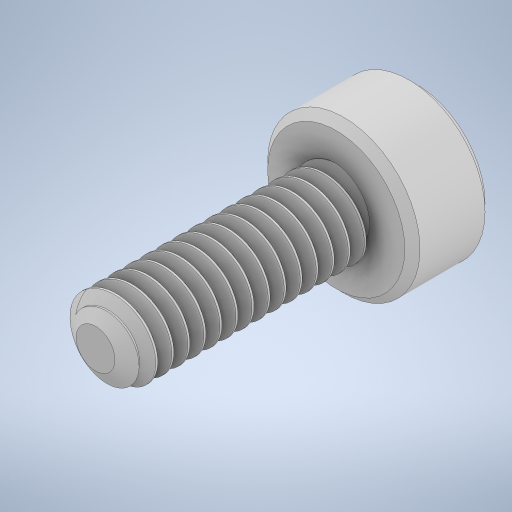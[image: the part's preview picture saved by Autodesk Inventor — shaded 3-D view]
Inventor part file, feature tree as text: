
AUTODESK INVENTOR PART (.ipt)
format: ipt  version: 2024 (Build 280153000, 153)  size: 736,768 bytes
history: native  units: mm
features: other x1, chamfer x1
ambient origin geometry x8: Origin, YZ Plane, XZ Plane, XY Plane, X Axis, Y Axis, Z Axis, Center Point
bodies: Body1 (feature_tree)
feature tree (2):
  other  "Těleso1"
  chamfer  "Chamfer1"  [1 undecoded]
note: 1 required parameter value undecoded (feature->parameter linkage not recoverable at this tier; creation-order binding heuristic only, values carry confidence <= 0.55)
